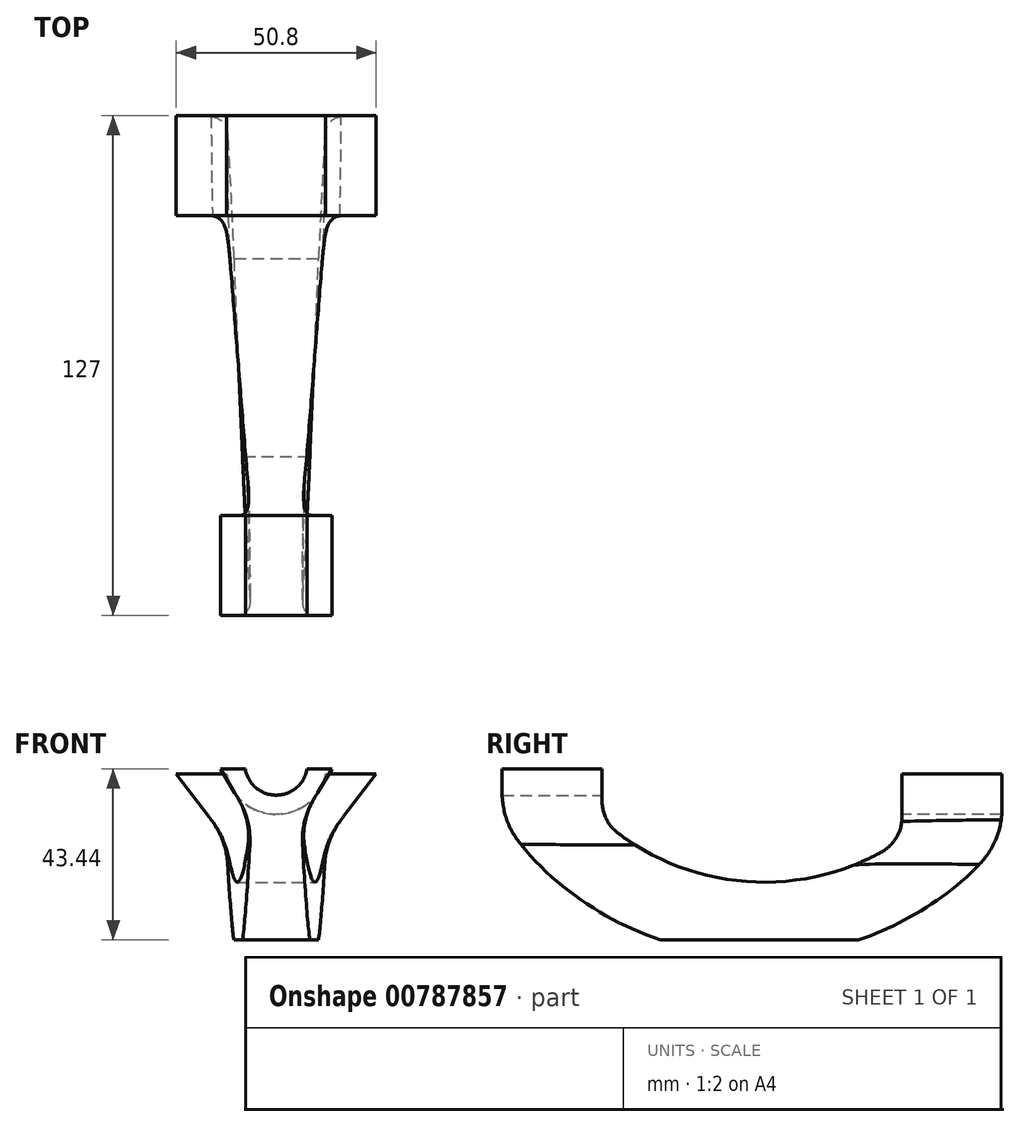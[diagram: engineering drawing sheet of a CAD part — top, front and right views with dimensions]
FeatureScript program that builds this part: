
annotation { "Feature Type Name" : "Feature", "Feature Type Description" : "" }
export const myFeature = defineFeature(function(context is Context, id is Id, definition is map)
    precondition{}
    {
        {
            var Q0;
            Q0=qCreatedBy(makeId("Front.planeOp"),FACE);
            var sketch = newSketch(context, id + "F0", { "sketchPlane" : qUnion([Q0])});
            skArc(sketch, "E0", {"start": v(-12.57, -2.54) * mm, "mid": v(0, -12.83) * mm, "end": v(12.57, -2.54) * mm});
            skLineSegment(sketch, "E1", {"start": v(12.57, -2.54) * mm, "end": v(25.4, -2.54) * mm});
            skLineSegment(sketch, "E2", {"start": v(25.4, -2.54) * mm, "end": v(12.7, -19.18) * mm});
            skLineSegment(sketch, "E3", {"start": v(12.7, -19.18) * mm, "end": v(-12.7, -19.18) * mm});
            skLineSegment(sketch, "E4", {"start": v(-12.7, -19.18) * mm, "end": v(-25.4, -2.54) * mm});
            skLineSegment(sketch, "E5", {"start": v(-25.4, -2.54) * mm, "end": v(-12.57, -2.54) * mm});
            skSolve(sketch);
        }
        {
            var Q0;
            Q0=qCreatedBy(makeId("Front.planeOp"),FACE);
            cPlane(context, id + "F1", {"entities" : qUnion([Q0]), "cplaneType" : CPlaneType.OFFSET, "offset" : 76.2 * mm, "width" : 152.4 * mm, "height" : 152.4 * mm});
        }
        {
            var Q0;
            Q0=qCreatedBy(id+"F1.planeOp",FACE);
            var sketch = newSketch(context, id + "F2", { "sketchPlane" : qUnion([Q0])});
            skArc(sketch, "E6", {"start": v(-7.84, -1.27) * mm, "mid": v(0, -7.94) * mm, "end": v(7.84, -1.27) * mm});
            skLineSegment(sketch, "E7", {"start": v(-7.84, -1.27) * mm, "end": v(-14.19, -1.27) * mm});
            skLineSegment(sketch, "E8", {"start": v(-14.19, -1.27) * mm, "end": v(-6.35, -14.29) * mm});
            skLineSegment(sketch, "E9", {"start": v(-6.35, -14.29) * mm, "end": v(6.35, -14.29) * mm});
            skLineSegment(sketch, "E10", {"start": v(6.35, -14.29) * mm, "end": v(14.19, -1.27) * mm});
            skLineSegment(sketch, "E11", {"start": v(14.19, -1.27) * mm, "end": v(7.84, -1.27) * mm});
            skSolve(sketch);
        }
        {
            var Q0;
            Q0=qSketchRegion(id+"F0",true);
            extrude(context, id + "F3", {"entities" : qUnion([Q0]), "oppositeDirection" : true, "depth" : 25.4 * mm, "offsetDistance" : 25.4 * mm});
        }
        {
            var Q0;
            Q0=qSketchRegion(id+"F2",true);
            extrude(context, id + "F4", {"entities" : qUnion([Q0]), "depth" : 25.4 * mm, "offsetDistance" : 25.4 * mm});
        }
        {
            var Q0;
            Q0=qCreatedBy(makeId("Right.planeOp"),FACE);
            var sketch = newSketch(context, id + "F5", { "sketchPlane" : qUnion([Q0])});
            skArc(sketch, "E12", {"start": v(-88.9, -14.29) * mm, "mid": v(-39.19, -39.33) * mm, "end": v(12.7, -19.18) * mm});
            skSolve(sketch);
        }
        {
            var Q0;
            Q0=sQuery(id+"F5.wireOp",EDGE,"E12");
            var Q1;
            Q1=makeQuery(id+"F3.opExtrude","SWEPT_FACE",FACE,{"disambiguationData":[OSD([sQuery(id+"F0.wireOp",EDGE,"E3")])]});
            var Q2;
            Q2=makeQuery(id+"F4.opExtrude","SWEPT_FACE",FACE,{"disambiguationData":[OSD([sQuery(id+"F2.wireOp",EDGE,"E9")])]});
            loft(context, id + "F6", {"addSections" : true, "spine" : qUnion([Q0]), "sectionCount" : 10, "sheetProfilesArray" : [{ "sheetProfileEntities" : qUnion([Q1]) }, { "sheetProfileEntities" : qUnion([Q2]) }]});
        }
        {
            var Q0;
            Q0=makeQuery(id+"F3.opExtrude","SWEPT_BODY",BODY,{"disambiguationData":[OSD([sQuery(id+"F0.wireOp",EDGE,"E0"),sQuery(id+"F0.wireOp",EDGE,"E1"),sQuery(id+"F0.wireOp",EDGE,"E2"),sQuery(id+"F0.wireOp",EDGE,"E3"),sQuery(id+"F0.wireOp",EDGE,"E4"),sQuery(id+"F0.wireOp",EDGE,"E5")])]});
            var Q1;
            Q1=makeQuery(id+"F4.opExtrude","SWEPT_BODY",BODY,{"disambiguationData":[OSD([sQuery(id+"F2.wireOp",EDGE,"E6"),sQuery(id+"F2.wireOp",EDGE,"E7"),sQuery(id+"F2.wireOp",EDGE,"E8"),sQuery(id+"F2.wireOp",EDGE,"E9"),sQuery(id+"F2.wireOp",EDGE,"E10"),sQuery(id+"F2.wireOp",EDGE,"E11")])]});
            var Q2;
            Q2=makeQuery(id+"F6.opLoft","SWEPT_BODY",BODY,{"disambiguationData":[OSD([sQuery(id+"F0.wireOp",EDGE,"E3"),sQuery(id+"F2.wireOp",EDGE,"E9")])]});
            booleanBodies(context, id + "F7", {"operationType" : BooleanOperationType.UNION, "tools" : qUnion([Q0, Q1, Q2])});
        }
        {
            var Q0;
            {var subQ0=sQuery(id+"F0.wireOp",EDGE,"E3");var subQ1=makeQuery(id+"F3.opExtrude","CAP_EDGE",EDGE,{"disambiguationData":[OSD([subQ0])],"isStart":true});var subQ2=sQuery(id+"F0.wireOp",EDGE,"E4");var subQ3=sQuery(id+"F0.wireOp",EDGE,"E2");Q0=makeQuery(id+"F7.opBoolean","MERGE",EDGE,{"derivedFrom":[subQ1,makeQuery(id+"F6.opLoft","MID_CAP_EDGE",EDGE,{"disambiguationData":[OSD([subQ3,subQ0,subQ2]),TDD([makeQuery(id+"F3.opExtrude","CAP_VERTEX",VERTEX,{"disambiguationData":[OSD([subQ3,subQ0])],"isStart":true}),makeQuery(id+"F3.opExtrude","CAP_VERTEX",VERTEX,{"disambiguationData":[OSD([subQ0,subQ2])],"isStart":true}),subQ1])],"capPos":0.0})]});}
            var Q1;
            {var subQ0=sQuery(id+"F2.wireOp",EDGE,"E9");var subQ1=makeQuery(id+"F4.opExtrude","CAP_EDGE",EDGE,{"disambiguationData":[OSD([subQ0])],"isStart":true});var subQ2=sQuery(id+"F2.wireOp",EDGE,"E10");var subQ3=sQuery(id+"F2.wireOp",EDGE,"E8");Q1=makeQuery(id+"F7.opBoolean","MERGE",EDGE,{"derivedFrom":[subQ1,makeQuery(id+"F6.opLoft","MID_CAP_EDGE",EDGE,{"disambiguationData":[OSD([subQ3,subQ0,subQ2]),TDD([makeQuery(id+"F4.opExtrude","CAP_VERTEX",VERTEX,{"disambiguationData":[OSD([subQ3,subQ0])],"isStart":true}),makeQuery(id+"F4.opExtrude","CAP_VERTEX",VERTEX,{"disambiguationData":[OSD([subQ0,subQ2])],"isStart":true}),subQ1])],"capPos":1.0})]});}
            fillet(context, id + "F8", {"entities" : qUnion([Q0, Q1]), "radius" : 10.16 * mm, "tangentPropagation" : true, "allowEdgeOverflow" : false});
        }
        {
            var Q0;
            {var subQ0=sQuery(id+"F0.wireOp",EDGE,"E4");var subQ1=sQuery(id+"F0.wireOp",EDGE,"E3");Q0=makeQuery(id+"F7.opBoolean","MERGE",EDGE,{"derivedFrom":[makeQuery(id+"F3.opExtrude","SWEPT_EDGE",EDGE,{"disambiguationData":[OSD([subQ1,subQ0])]}),makeQuery(id+"F6.opLoft","MID_CAP_EDGE",EDGE,{"disambiguationData":[OSD([subQ1,subQ0])],"capPos":0.0})]});}
            var Q1;
            {var subQ0=sQuery(id+"F0.wireOp",EDGE,"E3");var subQ1=sQuery(id+"F0.wireOp",EDGE,"E2");Q1=makeQuery(id+"F7.opBoolean","MERGE",EDGE,{"derivedFrom":[makeQuery(id+"F3.opExtrude","SWEPT_EDGE",EDGE,{"disambiguationData":[OSD([subQ1,subQ0])]}),makeQuery(id+"F6.opLoft","MID_CAP_EDGE",EDGE,{"disambiguationData":[OSD([subQ1,subQ0])],"capPos":0.0})]});}
            var Q2;
            {var subQ0=sQuery(id+"F0.wireOp",EDGE,"E3");var subQ1=makeQuery(id+"F3.opExtrude","CAP_EDGE",EDGE,{"disambiguationData":[OSD([subQ0])],"isStart":false});var subQ2=sQuery(id+"F0.wireOp",EDGE,"E4");var subQ3=sQuery(id+"F0.wireOp",EDGE,"E2");Q2=makeQuery(id+"F7.opBoolean","MERGE",EDGE,{"derivedFrom":[subQ1,makeQuery(id+"F6.opLoft","MID_CAP_EDGE",EDGE,{"disambiguationData":[OSD([subQ3,subQ0,subQ2]),TDD([makeQuery(id+"F3.opExtrude","CAP_VERTEX",VERTEX,{"disambiguationData":[OSD([subQ3,subQ0])],"isStart":false}),makeQuery(id+"F3.opExtrude","CAP_VERTEX",VERTEX,{"disambiguationData":[OSD([subQ0,subQ2])],"isStart":false}),subQ1])],"capPos":0.0})]});}
            var Q3;
            {var subQ0=sQuery(id+"F2.wireOp",EDGE,"E9");var subQ1=sQuery(id+"F2.wireOp",EDGE,"E8");Q3=makeQuery(id+"F7.opBoolean","MERGE",EDGE,{"derivedFrom":[makeQuery(id+"F4.opExtrude","SWEPT_EDGE",EDGE,{"disambiguationData":[OSD([subQ1,subQ0])]}),makeQuery(id+"F6.opLoft","MID_CAP_EDGE",EDGE,{"disambiguationData":[OSD([subQ1,subQ0])],"capPos":1.0})]});}
            var Q4;
            {var subQ0=sQuery(id+"F2.wireOp",EDGE,"E9");var subQ1=makeQuery(id+"F4.opExtrude","CAP_EDGE",EDGE,{"disambiguationData":[OSD([subQ0])],"isStart":false});var subQ2=sQuery(id+"F2.wireOp",EDGE,"E10");var subQ3=sQuery(id+"F2.wireOp",EDGE,"E8");Q4=makeQuery(id+"F7.opBoolean","MERGE",EDGE,{"derivedFrom":[subQ1,makeQuery(id+"F6.opLoft","MID_CAP_EDGE",EDGE,{"disambiguationData":[OSD([subQ3,subQ0,subQ2]),TDD([makeQuery(id+"F4.opExtrude","CAP_VERTEX",VERTEX,{"disambiguationData":[OSD([subQ3,subQ0])],"isStart":false}),makeQuery(id+"F4.opExtrude","CAP_VERTEX",VERTEX,{"disambiguationData":[OSD([subQ0,subQ2])],"isStart":false}),subQ1])],"capPos":1.0})]});}
            var Q5;
            {var subQ0=sQuery(id+"F2.wireOp",EDGE,"E10");var subQ1=sQuery(id+"F2.wireOp",EDGE,"E9");Q5=makeQuery(id+"F7.opBoolean","MERGE",EDGE,{"derivedFrom":[makeQuery(id+"F4.opExtrude","SWEPT_EDGE",EDGE,{"disambiguationData":[OSD([subQ1,subQ0])]}),makeQuery(id+"F6.opLoft","MID_CAP_EDGE",EDGE,{"disambiguationData":[OSD([subQ1,subQ0])],"capPos":1.0})]});}
            fillet(context, id + "F9", {"entities" : qUnion([Q0, Q1, Q2, Q3, Q4, Q5]), "radius" : 20.32 * mm, "tangentPropagation" : true, "allowEdgeOverflow" : false});
        }
        {
            var Q0;
            Q0=qCreatedBy(makeId("Front.planeOp"),FACE);
            var sketch = newSketch(context, id + "F10", { "sketchPlane" : qUnion([Q0])});
            skLineSegment(sketch, "E13.bottom", {"start": v(30.14, -57.98) * mm, "end": v(-44.9, -57.98) * mm});
            skLineSegment(sketch, "E13.top", {"start": v(30.14, -44.7) * mm, "end": v(-44.9, -44.7) * mm});
            skLineSegment(sketch, "E13.left", {"start": v(30.14, -57.98) * mm, "end": v(30.14, -44.7) * mm});
            skLineSegment(sketch, "E13.right", {"start": v(-44.9, -57.98) * mm, "end": v(-44.9, -44.7) * mm});
            skSolve(sketch);
        }
        {
            var Q0;
            Q0=qSketchRegion(id+"F10",true);
            extrude(context, id + "F11", {"entities" : qUnion([Q0]), "operationType" : NewBodyOperationType.REMOVE, "depth" : 116.08 * mm, "offsetDistance" : 25.4 * mm});
        }
    });
